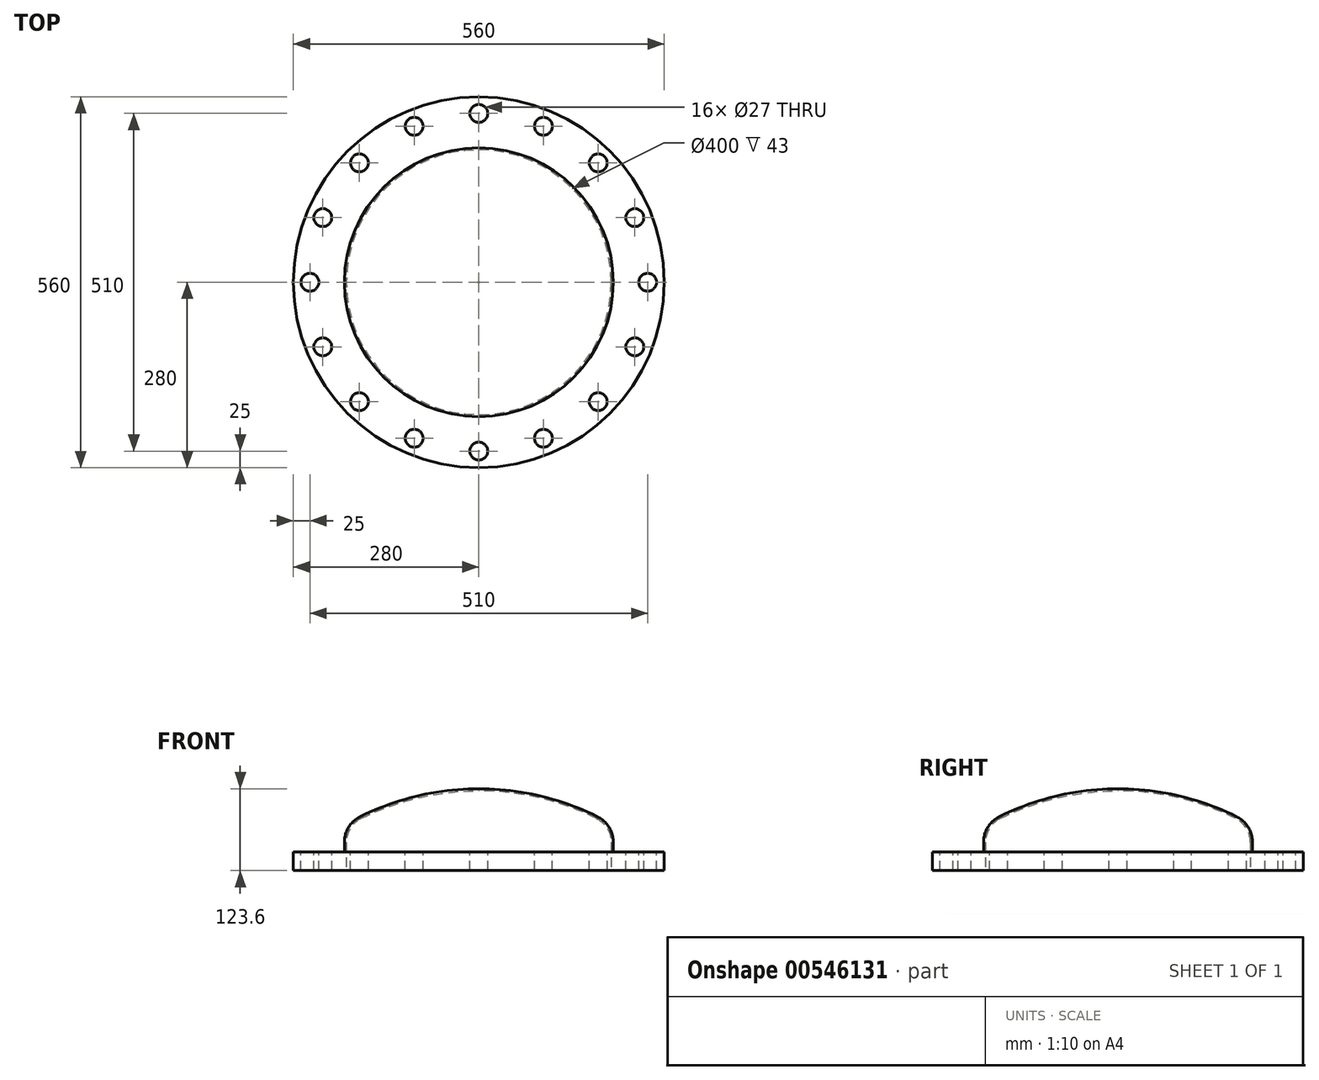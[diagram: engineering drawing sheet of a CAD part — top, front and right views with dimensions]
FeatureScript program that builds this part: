
annotation { "Feature Type Name" : "Feature", "Feature Type Description" : "" }
export const myFeature = defineFeature(function(context is Context, id is Id, definition is map)
    precondition{}
    {
        {
            var Q0;
            Q0=qCreatedBy(makeId("Front.planeOp"),FACE);
            var sketch = newSketch(context, id + "F0", { "sketchPlane" : qUnion([Q0])});
            skLineSegment(sketch, "E0", {"start": v(200, 0) * mm, "end": v(203, 0) * mm});
            skLineSegment(sketch, "E1", {"start": v(203, 0) * mm, "end": v(203, 20) * mm});
            skLineSegment(sketch, "E2", {"start": v(200, 0) * mm, "end": v(200, 20) * mm});
            skArc(sketch, "E3", {"start": v(200, 20) * mm, "mid": v(194, 41.07) * mm, "end": v(177.8, 55.82) * mm});
            skArc(sketch, "E4", {"start": v(177.8, 55.82) * mm, "mid": v(91.32, 87) * mm, "end": v(0, 97.6) * mm});
            skArc(sketch, "E5.0", {"start": v(179.13, 58.5) * mm, "mid": v(92, 89.92) * mm, "end": v(0, 100.6) * mm});
            skArc(sketch, "E5.1", {"start": v(203, 20) * mm, "mid": v(196.55, 42.65) * mm, "end": v(179.13, 58.5) * mm});
            skLineSegment(sketch, "E6", {"start": v(0, 97.6) * mm, "end": v(0, 100.6) * mm});
            skSolve(sketch);
        }
        {
            var Q0;
            Q0 = qSketchRegion(id + "F0", true);
            var Q1;
            Q1=sQuery(id+"F0.wireOp",EDGE,"E6");
            revolve(context, id + "F1", {"entities" : qUnion([Q0]), "axis" : qUnion([Q1]), "revolveType" : RevolveType.FULL});
        }
        {
            var Q0;
            Q0=makeQuery(id+"F1.opRevolve","SWEPT_FACE",FACE,{"disambiguationData":[OSD([sQuery(id+"F0.wireOp",EDGE,"E0")])]});
            var sketch = newSketch(context, id + "F2", { "sketchPlane" : qUnion([Q0])});
            skCircle(sketch, "E7", {"center": v(0, 0) * mm, "radius": 280 * mm});
            skCircle(sketch, "E8", {"center": v(0, 0) * mm, "radius": 200 * mm});
            skSolve(sketch);
        }
        {
            var Q0;
            Q0 = qSketchRegion(id + "F2", true);
            extrude(context, id + "F3", {"entities" : qUnion([Q0]), "operationType" : NewBodyOperationType.ADD, "depth" : 23 * mm, "offsetDistance" : 25 * mm, "hasSecondDirection" : true, "secondDirectionOppositeDirection" : true, "secondDirectionDepth" : 5 * mm});
        }
        {
            var Q0;
            Q0=makeQuery(id+"F3.opExtrude","CAP_FACE",FACE,{"disambiguationData":[OSD([sQuery(id+"F2.wireOp",EDGE,"E7"),sQuery(id+"F2.wireOp",EDGE,"E8")])],"isStart":true});
            var sketch = newSketch(context, id + "F4", { "sketchPlane" : qUnion([Q0])});
            skCircle(sketch, "E9", {"center": v(255, 0) * mm, "radius": 13.5 * mm});
            skCircle(sketch, "E10.1.0", {"center": v(235.59, 97.58) * mm, "radius": 13.5 * mm});
            skCircle(sketch, "E10.2.0", {"center": v(180.31, 180.31) * mm, "radius": 13.5 * mm});
            skCircle(sketch, "E10.3.0", {"center": v(97.58, 235.59) * mm, "radius": 13.5 * mm});
            skCircle(sketch, "E10.4.0", {"center": v(0, 255) * mm, "radius": 13.5 * mm});
            skCircle(sketch, "E10.5.0", {"center": v(-97.58, 235.59) * mm, "radius": 13.5 * mm});
            skCircle(sketch, "E10.6.0", {"center": v(-180.31, 180.31) * mm, "radius": 13.5 * mm});
            skCircle(sketch, "E10.7.0", {"center": v(-235.59, 97.58) * mm, "radius": 13.5 * mm});
            skCircle(sketch, "E10.8.0", {"center": v(-255, 0) * mm, "radius": 13.5 * mm});
            skCircle(sketch, "E10.9.0", {"center": v(-235.59, -97.58) * mm, "radius": 13.5 * mm});
            skCircle(sketch, "E10.10.0", {"center": v(-180.31, -180.31) * mm, "radius": 13.5 * mm});
            skCircle(sketch, "E10.11.0", {"center": v(-97.58, -235.59) * mm, "radius": 13.5 * mm});
            skCircle(sketch, "E10.12.0", {"center": v(0, -255) * mm, "radius": 13.5 * mm});
            skCircle(sketch, "E10.13.0", {"center": v(97.58, -235.59) * mm, "radius": 13.5 * mm});
            skCircle(sketch, "E10.14.0", {"center": v(180.31, -180.31) * mm, "radius": 13.5 * mm});
            skCircle(sketch, "E10.15.0", {"center": v(235.59, -97.58) * mm, "radius": 13.5 * mm});
            skPoint(sketch, "E10.center", {"position": v(0, 0) * mm});
            skSolve(sketch);
        }
        {
            var Q0;
            Q0 = qSketchRegion(id + "F4", true);
            extrude(context, id + "F5", {"entities" : qUnion([Q0]), "operationType" : NewBodyOperationType.REMOVE, "endBound" : BoundingType.UP_TO_NEXT, "oppositeDirection" : true, "depth" : 25 * mm, "offsetDistance" : 25 * mm});
        }
    });
